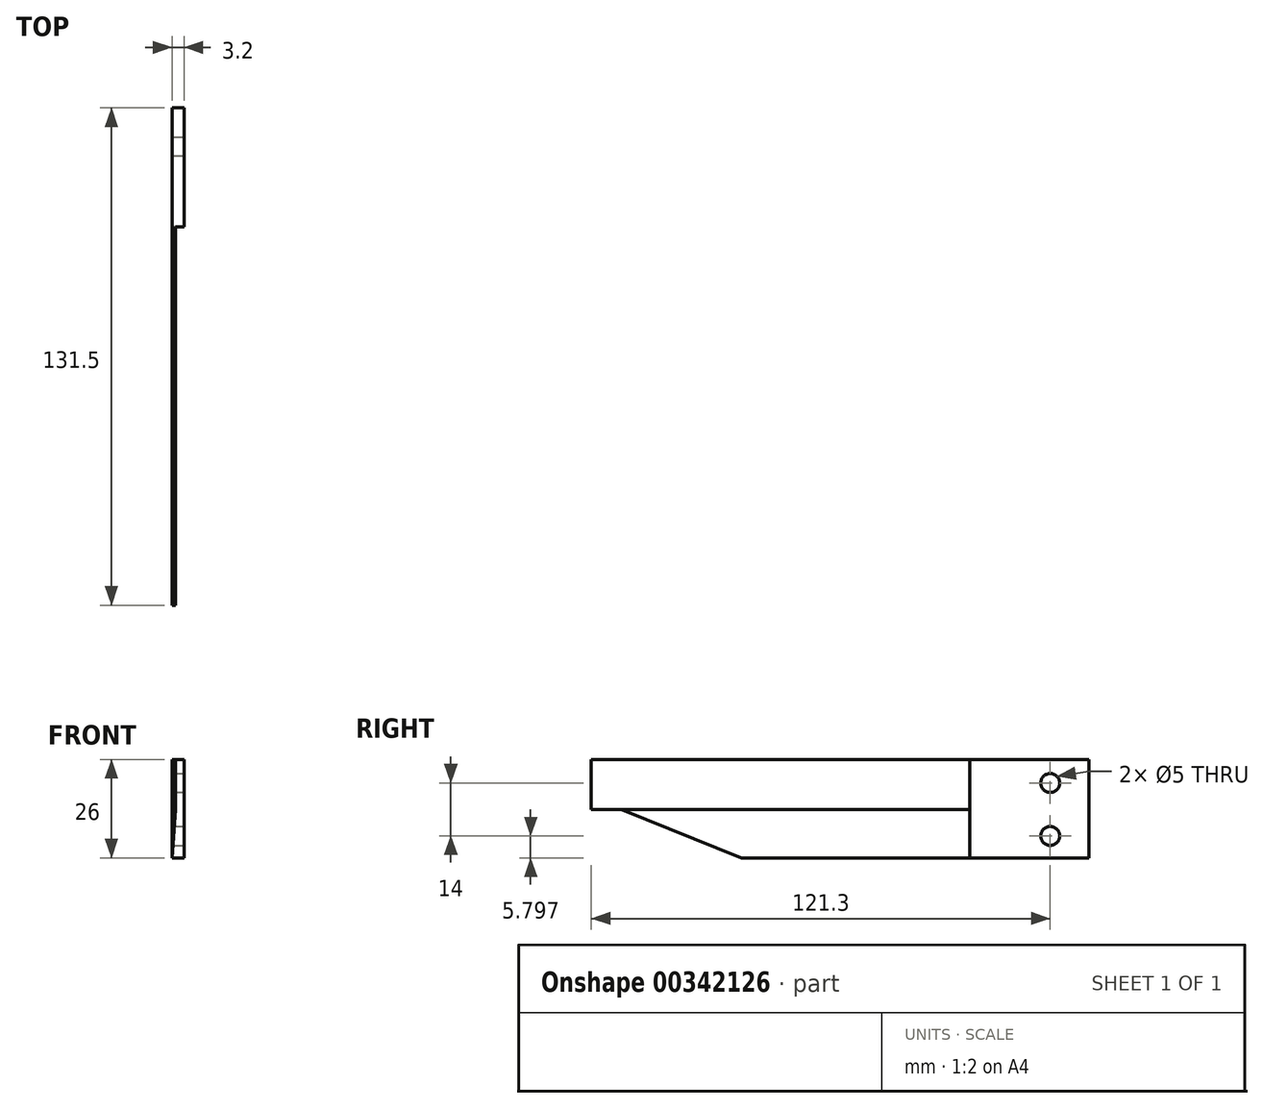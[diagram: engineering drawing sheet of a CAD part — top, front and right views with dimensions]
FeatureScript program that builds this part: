
annotation { "Feature Type Name" : "Feature", "Feature Type Description" : "" }
export const myFeature = defineFeature(function(context is Context, id is Id, definition is map)
    precondition{}
    {
        {
            var Q0;
            Q0=qCreatedBy(makeId("Front.planeOp"),FACE);
            var sketch = newSketch(context, id + "F0", { "sketchPlane" : qUnion([Q0])});
            skLineSegment(sketch, "E0.bottom", {"start": v(-9.66, 11.85) * mm, "end": v(-6.46, 11.85) * mm});
            skLineSegment(sketch, "E0.top", {"start": v(-9.66, -14.15) * mm, "end": v(-6.46, -14.15) * mm});
            skLineSegment(sketch, "E0.left", {"start": v(-9.66, 11.85) * mm, "end": v(-9.66, -14.15) * mm});
            skLineSegment(sketch, "E0.right", {"start": v(-6.46, 11.85) * mm, "end": v(-6.46, -14.15) * mm});
            skLineSegment(sketch, "E1", {"start": v(-6.46, -14.15) * mm, "end": v(-8.66, -14.15) * mm});
            skLineSegment(sketch, "E2", {"start": v(-8.66, -1.35) * mm, "end": v(-8.66, 11.85) * mm});
            skLineSegment(sketch, "E3", {"start": v(-8.66, 11.85) * mm, "end": v(-8.66, -1.35) * mm});
            skLineSegment(sketch, "E4", {"start": v(-9.66, -14.15) * mm, "end": v(-8.66, -1.35) * mm});
            skSolve(sketch);
        }
        {
            var Q0;
            Q0=qSketchRegion(id+"F0",true);
            extrude(context, id + "F1", {"entities" : qUnion([Q0]), "depth" : 31.5 * mm});
        }
        {
            var Q0;
            {var subQ0=sQuery(id+"F0.wireOp",EDGE,"E0.left");Q0=makeQuery(id+"F0.imprint","IMPRINT",FACE,{"disambiguationData":[TD([[makeQuery(id+"F0.imprint","IMPRINT",EDGE,{"derivedFrom":subQ0}),1.0]])]});}
            extrude(context, id + "F2", {"entities" : qUnion([Q0]), "operationType" : NewBodyOperationType.ADD, "depth" : 131.5 * mm});
        }
        {
            var Q0;
            Q0=makeQuery(id+"F2.opExtrude","CAP_VERTEX",VERTEX,{"disambiguationData":[OSD([sQuery(id+"F0.wireOp",EDGE,"E0.bottom"),sQuery(id+"F0.wireOp",EDGE,"E3")])],"isStart":false});
            var Q1;
            Q1=makeQuery(id+"F2.opExtrude","CAP_VERTEX",VERTEX,{"disambiguationData":[OSD([sQuery(id+"F0.wireOp",EDGE,"E0.bottom"),sQuery(id+"F0.wireOp",EDGE,"E0.left")])],"isStart":false});
            var Q2;
            Q2=makeQuery(id+"F2.opExtrude","CAP_VERTEX",VERTEX,{"disambiguationData":[OSD([sQuery(id+"F0.wireOp",EDGE,"E3"),sQuery(id+"F0.wireOp",EDGE,"E4")])],"isStart":false});
            cPlane(context, id + "F3", {"entities" : qUnion([Q0, Q1, Q2]), "cplaneType" : CPlaneType.THREE_POINT, "offset" : 25 * mm, "width" : 150 * mm, "height" : 150 * mm});
        }
        {
            var Q0;
            Q0=qCreatedBy(id+"F3.planeOp",FACE);
            var sketch = newSketch(context, id + "F4", { "sketchPlane" : qUnion([Q0])});
            skLineSegment(sketch, "E5.0.0", {"start": v(8.66, -1.35) * mm, "end": v(8.66, 11.85) * mm});
            skLineSegment(sketch, "E5.0.1", {"start": v(8.66, 11.85) * mm, "end": v(9.66, 11.85) * mm});
            skLineSegment(sketch, "E5.0.2", {"start": v(9.66, 11.85) * mm, "end": v(9.66, -14.15) * mm});
            skLineSegment(sketch, "E5.0.3", {"start": v(9.66, -14.15) * mm, "end": v(8.66, -1.35) * mm});
            skLineSegment(sketch, "E6.0", {"start": v(9.66, 11.85) * mm, "end": v(6.46, 11.85) * mm});
            skLineSegment(sketch, "E7.0", {"start": v(6.46, 11.85) * mm, "end": v(6.46, -14.15) * mm});
            skLineSegment(sketch, "E8.0", {"start": v(6.46, -14.15) * mm, "end": v(8.66, -14.15) * mm});
            skLineSegment(sketch, "E9.0", {"start": v(9.66, -14.15) * mm, "end": v(6.46, -14.15) * mm});
            skLineSegment(sketch, "E10", {"start": v(9.66, 11.85) * mm, "end": v(9.66, 6.05) * mm});
            skLineSegment(sketch, "E11", {"start": v(9.66, 6.05) * mm, "end": v(8.66, 6.05) * mm});
            skSolve(sketch);
        }
        {
            var Q0;
            Q0=qCreatedBy(makeId("Right.planeOp"),FACE);
            var sketch = newSketch(context, id + "F5", { "sketchPlane" : qUnion([Q0])});
            skLineSegment(sketch, "E12.0", {"start": v(-131.5, 11.85) * mm, "end": v(0, 11.85) * mm});
            skPoint(sketch, "E13.0", {"position": v(-131.5, 6.05) * mm});
            skLineSegment(sketch, "E14.0", {"start": v(-131.5, 11.85) * mm, "end": v(-131.5, -14.15) * mm});
            skLineSegment(sketch, "E15.0", {"start": v(-131.5, -14.15) * mm, "end": v(-31.5, -14.15) * mm});
            skLineSegment(sketch, "E16", {"start": v(-131.5, -1.35) * mm, "end": v(-123.5, -1.35) * mm});
            skLineSegment(sketch, "E17", {"start": v(-131.5, -1.35) * mm, "end": v(-131.5, 6.65) * mm});
            skLineSegment(sketch, "E18", {"start": v(-123.5, -1.35) * mm, "end": v(-131.5, 6.65) * mm});
            skLineSegment(sketch, "E19", {"start": v(-123.5, -14.15) * mm, "end": v(-131.5, -14.15) * mm});
            skLineSegment(sketch, "E20", {"start": v(-31.5, -14.15) * mm, "end": v(-91.82, -14.15) * mm});
            skLineSegment(sketch, "E21", {"start": v(-91.82, -14.15) * mm, "end": v(-123.5, -1.35) * mm});
            skLineSegment(sketch, "E22.0", {"start": v(0, 11.85) * mm, "end": v(0, -1.35) * mm});
            skPoint(sketch, "E23.0", {"position": v(0, -7.75) * mm});
            skLineSegment(sketch, "E24.0", {"start": v(-31.5, 11.85) * mm, "end": v(-31.5, -14.15) * mm});
            skLineSegment(sketch, "E25.0.0", {"start": v(0, -14.15) * mm, "end": v(0, 11.85) * mm});
            skLineSegment(sketch, "E25.0.1", {"start": v(0, 11.85) * mm, "end": v(-31.5, 11.85) * mm});
            skLineSegment(sketch, "E25.0.3", {"start": v(-31.5, -14.15) * mm, "end": v(0, -14.15) * mm});
            skLineSegment(sketch, "E26", {"start": v(0, -1.35) * mm, "end": v(-10.2, -1.35) * mm});
            skLineSegment(sketch, "E27", {"start": v(-10.2, -1.35) * mm, "end": v(-10.2, 5.65) * mm});
            skLineSegment(sketch, "E28", {"start": v(-10.2, -1.35) * mm, "end": v(-10.2, -8.35) * mm});
            skSolve(sketch);
        }
        {
            var Q0;
            {var subQ2=sQuery(id+"F5.wireOp",EDGE,"E16");Q0=makeQuery(id+"F5.imprint","IMPRINT",FACE,{"disambiguationData":[TD([[makeQuery(id+"F5.imprint","IMPRINT",EDGE,{"derivedFrom":subQ2}),-1.0]])]});}
            var Q1;
            Q1=makeQuery(id+"F5.imprint","IMPRINT",FACE,{"disambiguationData":[TD([[makeQuery(id+"F5.imprint","IMPRINT",EDGE,{"derivedFrom":sQuery(id+"F5.wireOp",EDGE,"E17")}),-1.0]])]});
            var Q2;
            Q2=makeQuery(id+"F5.imprint","IMPRINT",FACE,{"disambiguationData":[TD([[makeQuery(id+"F5.imprint","IMPRINT",EDGE,{"derivedFrom":sQuery(id+"F5.wireOp",EDGE,"E15.0")}),1.0]])]});
            extrude(context, id + "F6", {"entities" : qUnion([Q0, Q1, Q2]), "operationType" : NewBodyOperationType.REMOVE, "oppositeDirection" : true, "depth" : 25 * mm});
        }
        {
            var Q0;
            Q0=sQuery(id+"F5.wireOp",VERTEX,"E27.end");
            var Q1;
            Q1=sQuery(id+"F5.wireOp",VERTEX,"E28.end");
            var Q2;
            Q2=makeQuery(id+"F1.opExtrude","SWEPT_BODY",BODY,{"disambiguationData":[OSD([sQuery(id+"F0.wireOp",EDGE,"E0.bottom"),sQuery(id+"F0.wireOp",EDGE,"E0.top"),sQuery(id+"F0.wireOp",EDGE,"E0.left"),sQuery(id+"F0.wireOp",EDGE,"E0.right"),sQuery(id+"F0.wireOp",EDGE,"E1")])]});
            hole(context, id + "F7", {"style" : HoleStyle.SIMPLE, "endStyle" : HoleEndStyle.BLIND, "holeDiameter" : 5 * mm, "holeDepth" : 300 * mm, "tappedDepth" : 12 * mm, "tapClearance" : 3, "locations" : qUnion([Q0, Q1]), "scope" : qUnion([Q2])});
        }
    });
